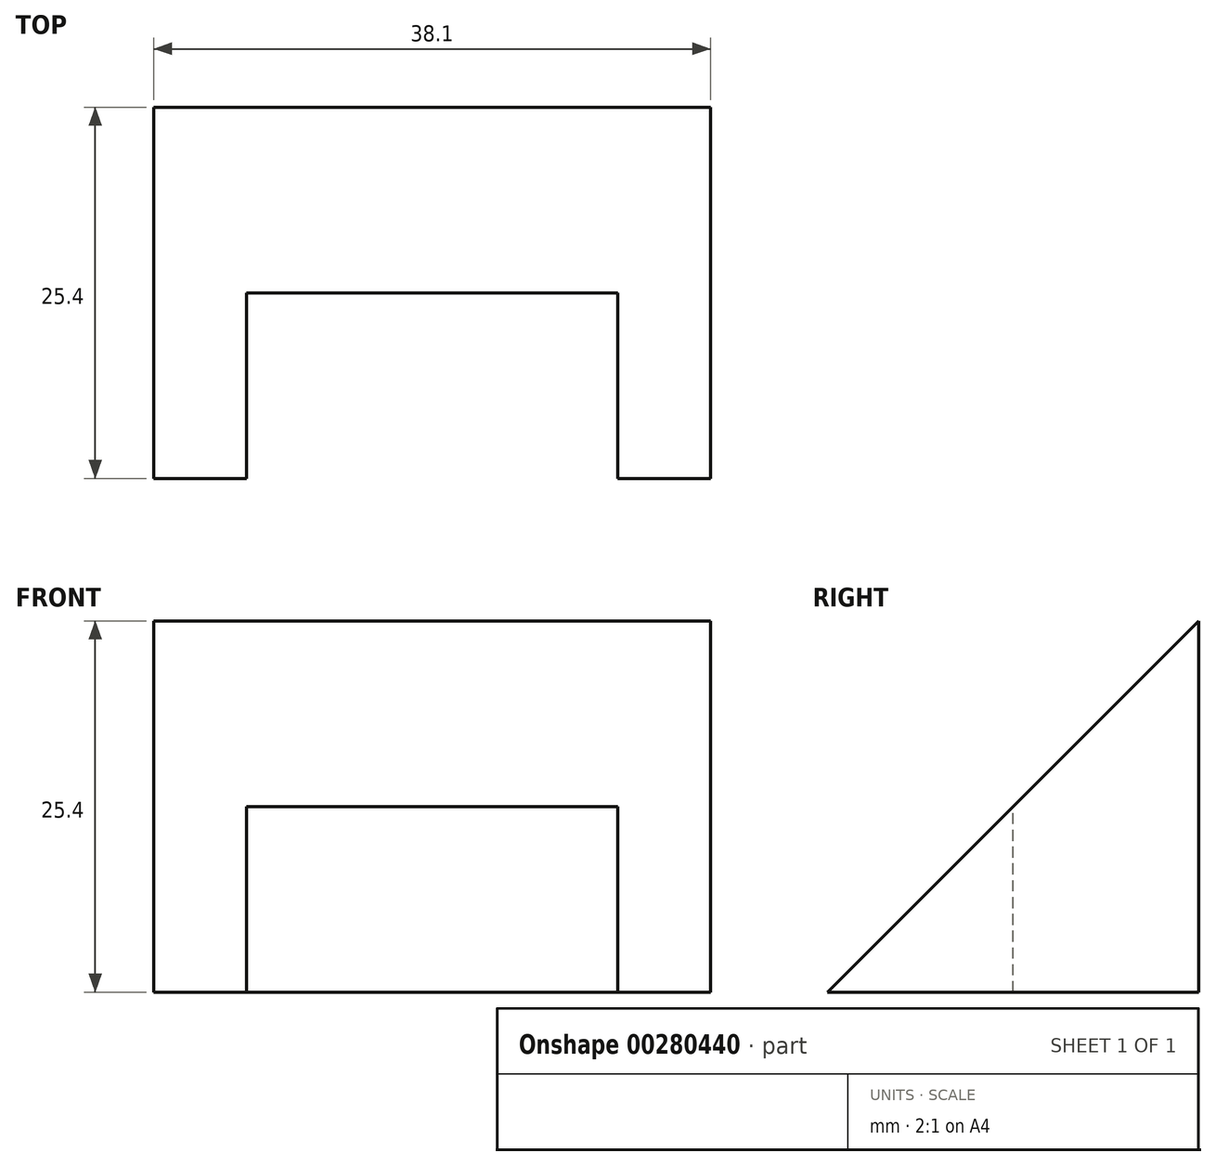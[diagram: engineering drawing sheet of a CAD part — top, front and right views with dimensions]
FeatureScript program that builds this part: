
annotation { "Feature Type Name" : "Feature", "Feature Type Description" : "" }
export const myFeature = defineFeature(function(context is Context, id is Id, definition is map)
    precondition{}
    {
        {
            var Q0;
            Q0=qCreatedBy(makeId("Right.planeOp"),FACE);
            var sketch = newSketch(context, id + "F0", { "sketchPlane" : qUnion([Q0])});
            skLineSegment(sketch, "E0.bottom", {"start": v(0, 0) * mm, "end": v(-25.4, 0) * mm});
            skLineSegment(sketch, "E0.top", {"start": v(0, 25.4) * mm, "end": v(-25.4, 25.4) * mm});
            skLineSegment(sketch, "E0.left", {"start": v(0, 0) * mm, "end": v(0, 25.4) * mm});
            skLineSegment(sketch, "E0.right", {"start": v(-25.4, 0) * mm, "end": v(-25.4, 25.4) * mm});
            skSolve(sketch);
        }
        {
            var Q0;
            Q0 = qSketchRegion(id + "F0", true);
            extrude(context, id + "F1", {"entities" : qUnion([Q0]), "endBound" : BoundingType.SYMMETRIC, "depth" : 38.1 * mm});
        }
        {
            var Q0;
            Q0=qCreatedBy(makeId("Right.planeOp"),FACE);
            var sketch = newSketch(context, id + "F2", { "sketchPlane" : qUnion([Q0])});
            skLineSegment(sketch, "E1", {"start": v(-25.4, 25.4) * mm, "end": v(0, 25.4) * mm});
            skLineSegment(sketch, "E2", {"start": v(0, 25.4) * mm, "end": v(-25.4, 0) * mm});
            skLineSegment(sketch, "E3", {"start": v(-25.4, 0) * mm, "end": v(-25.4, 25.4) * mm});
            skSolve(sketch);
        }
        {
            var Q0;
            Q0 = qSketchRegion(id + "F2", true);
            extrude(context, id + "F3", {"entities" : qUnion([Q0]), "operationType" : NewBodyOperationType.REMOVE, "endBound" : BoundingType.SYMMETRIC, "oppositeDirection" : true, "depth" : 38.1 * mm});
        }
        {
            var Q0;
            Q0=qCreatedBy(makeId("Right.planeOp"),FACE);
            var sketch = newSketch(context, id + "F4", { "sketchPlane" : qUnion([Q0])});
            skLineSegment(sketch, "E4", {"start": v(-12.7, 12.7) * mm, "end": v(-25.4, 0) * mm});
            skLineSegment(sketch, "E5", {"start": v(-25.4, 0) * mm, "end": v(-12.7, 0) * mm});
            skLineSegment(sketch, "E6", {"start": v(-12.7, 0) * mm, "end": v(-12.7, 12.7) * mm});
            skSolve(sketch);
        }
        {
            var Q0;
            Q0 = qSketchRegion(id + "F4", true);
            extrude(context, id + "F5", {"entities" : qUnion([Q0]), "operationType" : NewBodyOperationType.REMOVE, "endBound" : BoundingType.SYMMETRIC, "oppositeDirection" : true, "depth" : 25.4 * mm});
        }
    });
